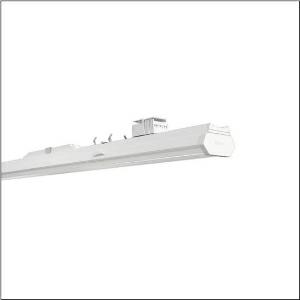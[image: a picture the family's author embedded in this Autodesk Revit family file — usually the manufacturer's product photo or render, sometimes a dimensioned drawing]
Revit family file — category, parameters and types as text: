
# Revit family: licross_r__21_protected_ho_52td12dn4e5m3s_02cf
name_source: partatom
category: Lighting Fixtures
units: mm (PartAtom-declared; Revit-internal decimal feet)

## family parameters
Cut with Voids When Loaded = No
Host = Face
Light Source = No
Part Type = Normal
Room Calculation Point = No
Round Connector Dimension = Use Diameter
Shared = No

## types (1)
- --- (1 x LED, 910 lm, 7.6 W, 4000K)
    Apparent Load = 8 VA
    CIE Flux Codes = 70 91 97 98 100
    Color Rendering = 80
    Color Temperature = 4000K
    Default Elevation = 1800 mm
    Description = Licross® 21 Protected HO, luminaire insert, of sheet steel, galvanised, coil coated, white, length: 1.500mm, width: 90mm, height: 103mm, LED rated luminous flux: 14.690lm, light colour: 840, control gear: DALI 2 (for two DALI lines), with plug, 6-pole, with phase selection, for trunking rail, 14-core, mains connection: 220..240V, AC, 50/60Hz, rated input power: 89W, for trunking rail, 14-core, halogen-free wiring, for emergency light function, converter,control gear: single battery element, battery: LiFePO4, 9Ah, primary light control with lens, of plastic, primary optical cover: cover, of PMMA, light emission: direct distribution, primary light characteristic: symmetric, protection rating (complete): IP54, insulation class (complete): insulation class I (protective earthing), certification: CE, UKCA, protection symbol: D if used in an environment with non-conductive dust loads with corresponding accessories, impact resistance: IK06, permissible ambient temperature for indoor applications: +5..+30°C, standard: EN 60598-2-22, LABS conformity tested according to VDMA 24364:2018-05, reducing of maximum allowable ambient temperature of 5°C with ceiling mounting, corresponds to IFS (International Featured Standards) requirements for safety and quality in the food industry, packaging unit: 1 piece
    Height = 92 mm
    Lamp = 1 x LED
    Lamp Light Flux = 910 lm
    Lamp Power = 7.6 W
    Lamp count = 1
    Length = 1500 mm
    Luminous efficacy = 120 lm/W
    Manufacturer = Siteco
    ModVariant = No
    Model = 52TD12DN4E5M3S
    Mounting Place = Ceiling
    Mounting Type = Pendant
    Number of Poles = 1
    OnlyDefault = Yes
    Power Factor = 1
    Product Name = Licross® 21 Protected HO
    Product group = luminaire insert
    ProductGroupID = 902
    Protection Class = Protection class I
    Protection Degree = IP 54
    RLX_Detail_Level = 1
    RLX_Emergency_Light_Flux = 0 lm
    RLX_Emergency_Type = 0
    RLX_Emergency_Type_DB = No
    RlxData = <blob elided: 24853 chars, md5=9a6c5486>
    Socket = socket
    Standby Power = 0 W
    System Light Flux = 910 lm
    System Power = 8 W
    Type Comments = : emergency light operation: 3 h
    Type Image = l_1256148.jpg
    URL = http://relux.com
    VarID = @adj_111232
    Voltage = 0 V
    Weight = 0.00 kg
    Width = 88 mm

## geometry (parser evidence)
native form markers: Blend x4, Sweep x11
no freeform markers — native parametric forms only
